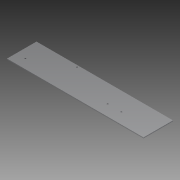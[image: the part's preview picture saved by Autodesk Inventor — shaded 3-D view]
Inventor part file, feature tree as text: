
AUTODESK INVENTOR PART (.ipt)
format: ipt  version: 2013 (Build 170138000, 138)  size: 84,992 bytes
history: native  units: in
note: dims shown in document units (in); Inventor stores cm internally (conversion verified against a paired STEP export)
features: extrude x1, sketch x1
ambient origin geometry x8: Origin, YZ Plane, XZ Plane, XY Plane, X Axis, Y Axis, Z Axis, Center Point
bodies: Solid1 (feature_tree)
feature tree (2):
  extrude  "Extrusion1"  Depth=4.0in
  sketch  "Sketch1"  dims[d0=18.5in d2=4.0in d3=0.2in d5=2.5in d6=1.25in d7=0.25in d8=1.86in d9=0.2in d10=2.5in d11=4.5in d12=0.125in d13=0.0in d16=4.5in]
